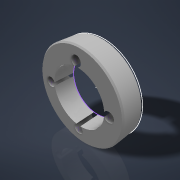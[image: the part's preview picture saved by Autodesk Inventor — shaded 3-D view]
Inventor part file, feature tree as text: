
AUTODESK INVENTOR PART (.ipt)
format: ipt  version: 2022 (Build 260153070, 153G)  size: 139,776 bytes
history: native  units: mm
features: sketch x2, other x1, extrude x1, chamfer x1, hole x1
ambient origin geometry x8: Origin, YZ Plane, XZ Plane, XY Plane, X Axis, Y Axis, Z Axis, Center Point
bodies: Body1 (feature_tree)
feature tree (6):
  other  "Твердое тело1"
  sketch  "Эскиз1"
  extrude  "Выдавливание1"  Depth=17.0mm TaperAngle=0.0deg
  chamfer  "Фаска1"  Distance=1.0mm Angle=45.0deg
  sketch  "Эскиз2"
  hole  "Отверстие1"  [1 undecoded]
note: 1 required parameter value undecoded (feature->parameter linkage not recoverable at this tier; creation-order binding heuristic only, values carry confidence <= 0.55)
